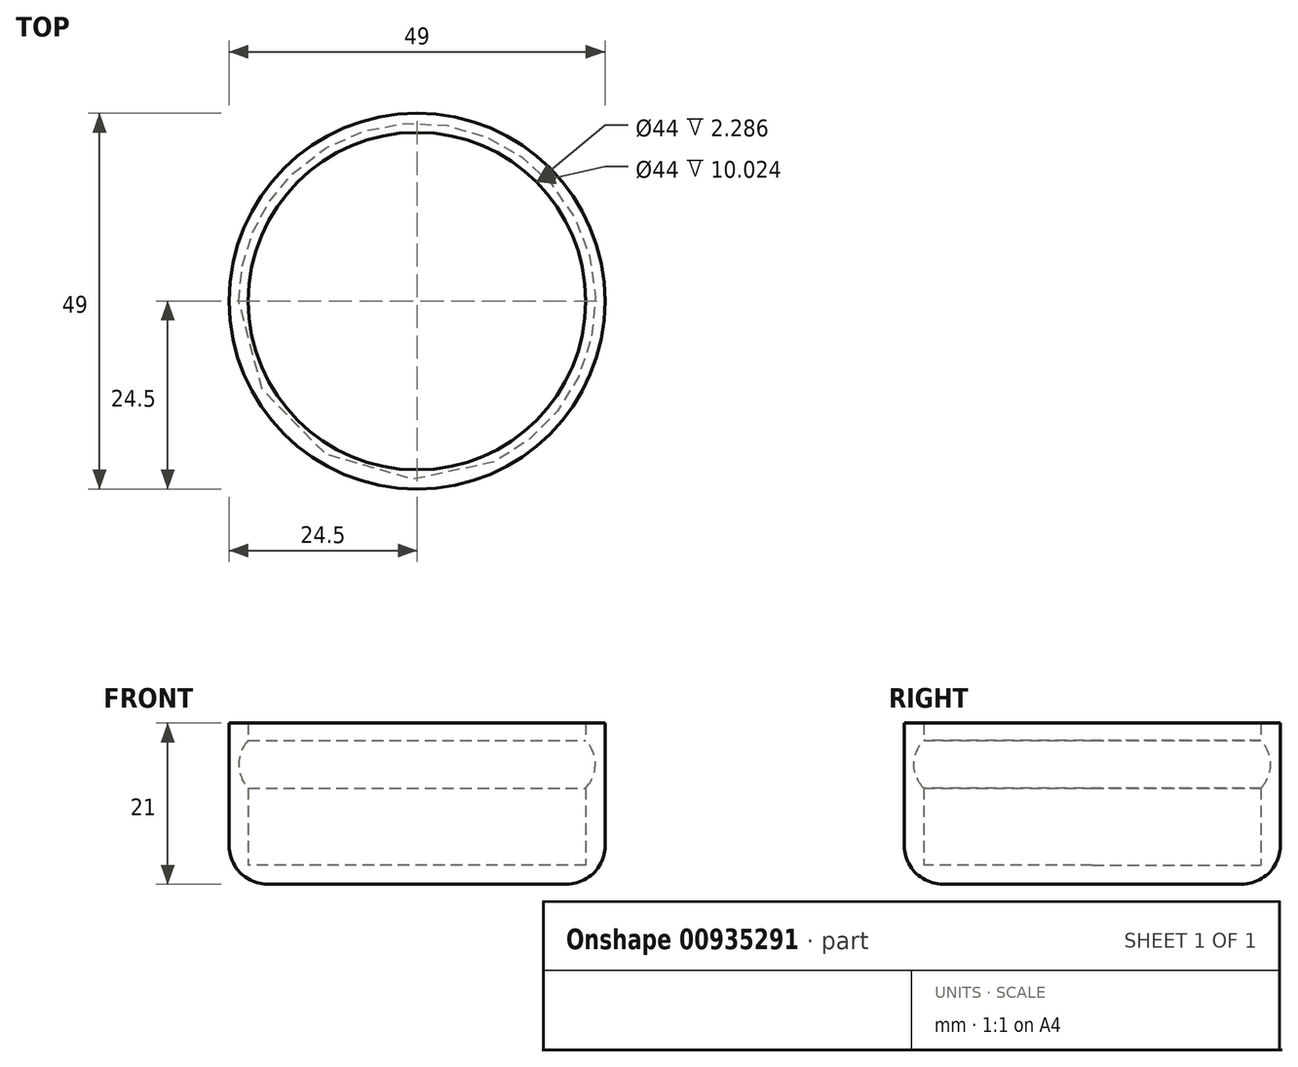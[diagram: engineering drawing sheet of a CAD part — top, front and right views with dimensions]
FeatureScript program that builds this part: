
annotation { "Feature Type Name" : "Feature", "Feature Type Description" : "" }
export const myFeature = defineFeature(function(context is Context, id is Id, definition is map)
    precondition{}
    {
        {
            var Q0;
            Q0=qCreatedBy(makeId("Top.planeOp"),FACE);
            var sketch = newSketch(context, id + "F0", { "sketchPlane" : qUnion([Q0])});
            skCircle(sketch, "E0", {"center": v(0, 0) * mm, "radius": 24.5 * mm});
            skSolve(sketch);
        }
        {
            var Q0;
            Q0=makeQuery(id+"F0.imprint","IMPRINT",FACE,{"disambiguationData":[TD([[makeQuery(id+"F0.imprint","IMPRINT",EDGE,{"derivedFrom":sQuery(id+"F0.wireOp",EDGE,"E0")}),1.0]])]});
            extrude(context, id + "F1", {"entities" : qUnion([Q0]), "endBound" : BoundingType.SYMMETRIC, "depth" : 21 * mm, "offsetDistance" : 25 * mm});
        }
        {
            var Q0;
            Q0=makeQuery(id+"F1.opExtrude","CAP_FACE",FACE,{"disambiguationData":[OSD([sQuery(id+"F0.wireOp",EDGE,"E0")])],"isStart":false});
            shell(context, id + "F2", {"entities" : qUnion([Q0]), "thickness" : 2.5 * mm});
        }
        {
            var Q0;
            Q0=qCreatedBy(makeId("Front.planeOp"),FACE);
            var sketch = newSketch(context, id + "F3", { "sketchPlane" : qUnion([Q0])});
            skArc(sketch, "E1", {"start": v(-22, 8.21) * mm, "mid": v(-23.24, 5.12) * mm, "end": v(-22, 2.02) * mm});
            skLineSegment(sketch, "E2", {"start": v(-22, 8.21) * mm, "end": v(-22, 2.02) * mm});
            skLineSegment(sketch, "E3", {"start": v(0, 13.74) * mm, "end": v(0, -7.06) * mm, "construction": true});
            skLineSegment(sketch, "E4.0", {"start": v(-22, 10.5) * mm, "end": v(22, 10.5) * mm});
            skSolve(sketch);
        }
        {
            var Q0;
            Q0=makeQuery(id+"F3.imprint","IMPRINT",FACE,{"disambiguationData":[TD([[makeQuery(id+"F3.imprint","IMPRINT",EDGE,{"derivedFrom":sQuery(id+"F3.wireOp",EDGE,"E1")}),1.0]])]});
            var Q1;
            Q1=sQuery(id+"F3.wireOp",EDGE,"E3");
            revolve(context, id + "F4", {"operationType" : NewBodyOperationType.REMOVE, "surfaceOperationType" : NewSurfaceOperationType.NEW, "entities" : qUnion([Q0]), "axis" : qUnion([Q1]), "revolveType" : RevolveType.FULL, "oppositeDirection" : true});
        }
        {
            var Q0;
            Q0=makeQuery(id+"F1.opExtrude","CAP_EDGE",EDGE,{"disambiguationData":[OSD([sQuery(id+"F0.wireOp",EDGE,"E0")])],"isStart":true});
            fillet(context, id + "F5", {"entities" : qUnion([Q0]), "radius" : 5 * mm, "tangentPropagation" : true, "allowEdgeOverflow" : false});
        }
    });
